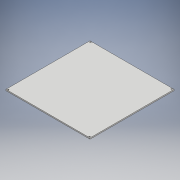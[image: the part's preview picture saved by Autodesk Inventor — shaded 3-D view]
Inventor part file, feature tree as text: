
AUTODESK INVENTOR PART (.ipt)
format: ipt  version: 2017 (Build 210142000, 142)  size: 105,984 bytes
history: native  units: mm
features: extrude x2, sketch x2, projected_geometry x1
ambient origin geometry x8: Origin, YZ Plane, XZ Plane, XY Plane, X Axis, Y Axis, Z Axis, Center Point
bodies: Solid1 (feature_tree)
feature tree (5):
  extrude  "Extrusion1"  Depth=3.0mm TaperAngle=0.0deg
  extrude  "Extrusion2"  Depth=3.0mm
  sketch  "Sketch1"  dims[d0=213.0mm d1=3.0mm d2=0.0mm]
  sketch  "Sketch2"  dims[d3=3.0mm d4=2.0mm d5=1.0mm d6=3.0mm d7=0.0mm]
  projected_geometry  "Projected Loop1"
